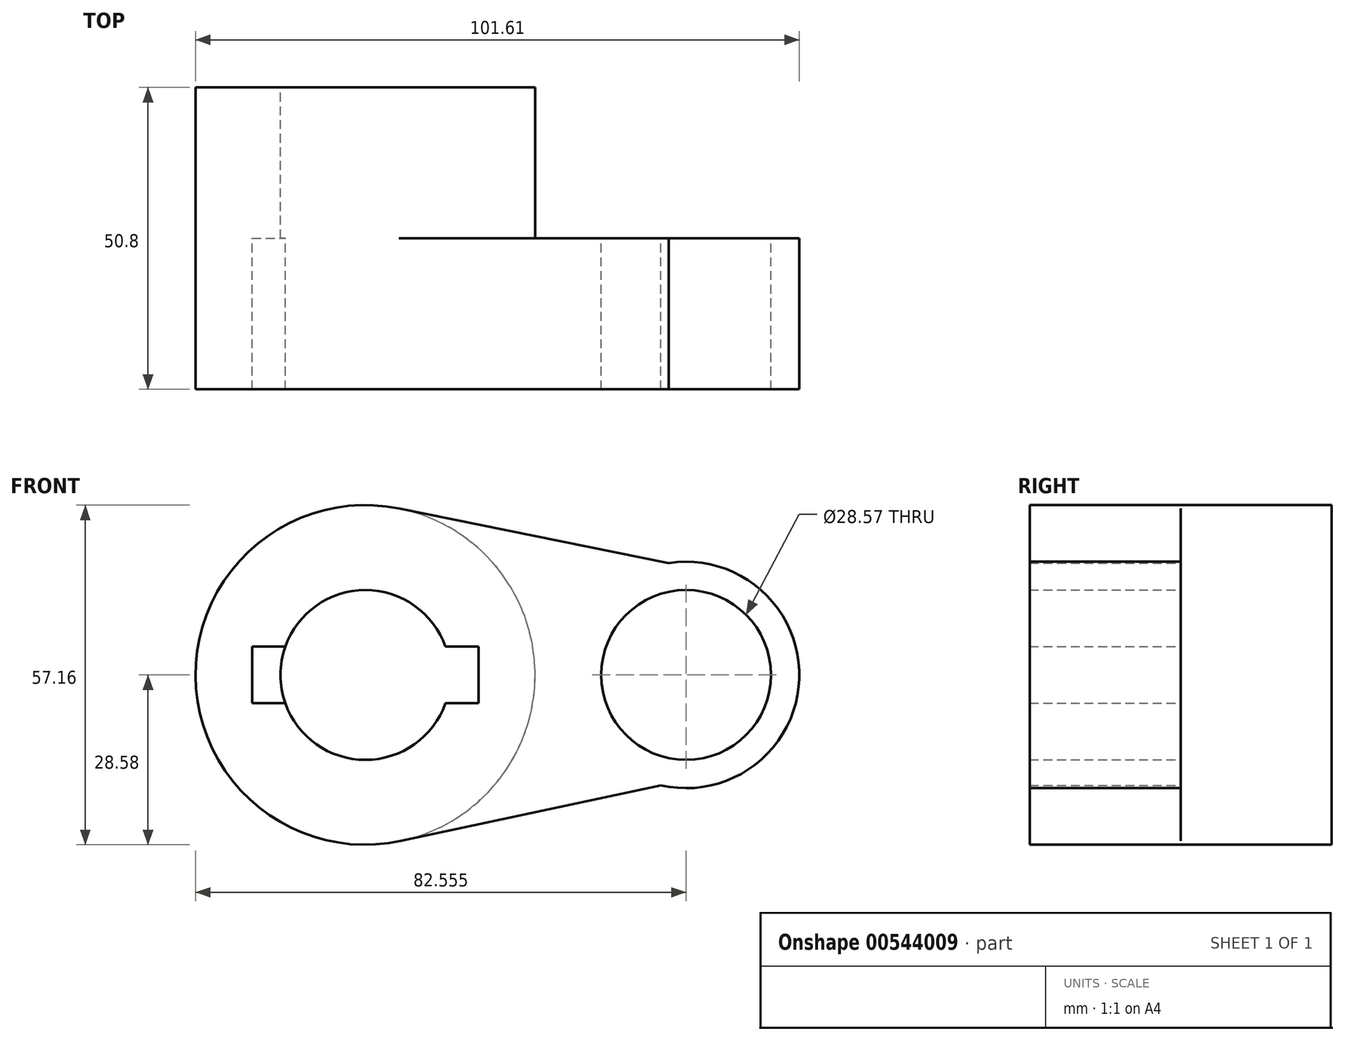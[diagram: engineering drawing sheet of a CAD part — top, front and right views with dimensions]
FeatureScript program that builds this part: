
annotation { "Feature Type Name" : "Feature", "Feature Type Description" : "" }
export const myFeature = defineFeature(function(context is Context, id is Id, definition is map)
    precondition{}
    {
        {
            var Q0;
            Q0=qCreatedBy(makeId("Front.planeOp"),FACE);
            var sketch = newSketch(context, id + "F0", { "sketchPlane" : qUnion([Q0])});
            skCircle(sketch, "E0", {"center": v(0, 0) * mm, "radius": 28.58 * mm});
            skCircle(sketch, "E1", {"center": v(53.98, 0) * mm, "radius": 19.05 * mm});
            skLineSegment(sketch, "E2", {"start": v(5.67, 28) * mm, "end": v(51.04, 18.82) * mm});
            skLineSegment(sketch, "E3", {"start": v(5.98, -27.94) * mm, "end": v(49.74, -18.57) * mm});
            skCircle(sketch, "E4", {"center": v(0, 0) * mm, "radius": 14.29 * mm});
            skCircle(sketch, "E5", {"center": v(53.98, 0) * mm, "radius": 14.29 * mm});
            skLineSegment(sketch, "E6.bottom", {"start": v(-19.05, 4.76) * mm, "end": v(19.05, 4.76) * mm});
            skLineSegment(sketch, "E6.top", {"start": v(-19.05, -4.76) * mm, "end": v(19.05, -4.76) * mm});
            skLineSegment(sketch, "E6.left", {"start": v(-19.05, 4.76) * mm, "end": v(-19.05, -4.76) * mm});
            skLineSegment(sketch, "E6.right", {"start": v(19.05, 4.76) * mm, "end": v(19.05, -4.76) * mm});
            skSolve(sketch);
        }
        {
            var Q0;
            {var subQ7=sQuery(id+"F0.wireOp",EDGE,"E6.left");Q0=makeQuery(id+"F0.imprint","IMPRINT",FACE,{"disambiguationData":[TD([[makeQuery(id+"F0.imprint","IMPRINT",EDGE,{"derivedFrom":subQ7}),-1.0]])]});}
            var Q1;
            {var subQ0=sQuery(id+"F0.wireOp",EDGE,"E2");Q1=makeQuery(id+"F0.imprint","IMPRINT",FACE,{"disambiguationData":[TD([[makeQuery(id+"F0.imprint","IMPRINT",EDGE,{"derivedFrom":subQ0}),-1.0]])]});}
            var Q2;
            Q2=makeQuery(id+"F0.imprint","IMPRINT",FACE,{"disambiguationData":[TD([[makeQuery(id+"F0.imprint","IMPRINT",EDGE,{"derivedFrom":sQuery(id+"F0.wireOp",EDGE,"E5")}),-1.0]])]});
            extrude(context, id + "F1", {"entities" : qUnion([Q0, Q1, Q2]), "depth" : 25.4 * mm, "offsetDistance" : 25.4 * mm});
        }
        {
            var Q0;
            {var subQ5=sQuery(id+"F0.wireOp",EDGE,"E6.left");Q0=makeQuery(id+"F0.imprint","IMPRINT",FACE,{"disambiguationData":[TD([[makeQuery(id+"F0.imprint","IMPRINT",EDGE,{"derivedFrom":subQ5}),1.0]])]});}
            var Q1;
            {var subQ7=sQuery(id+"F0.wireOp",EDGE,"E6.left");Q1=makeQuery(id+"F0.imprint","IMPRINT",FACE,{"disambiguationData":[TD([[makeQuery(id+"F0.imprint","IMPRINT",EDGE,{"derivedFrom":subQ7}),-1.0]])]});}
            extrude(context, id + "F2", {"entities" : qUnion([Q0, Q1]), "operationType" : NewBodyOperationType.ADD, "oppositeDirection" : true, "depth" : 25.4 * mm, "offsetDistance" : 25.4 * mm});
        }
    });
